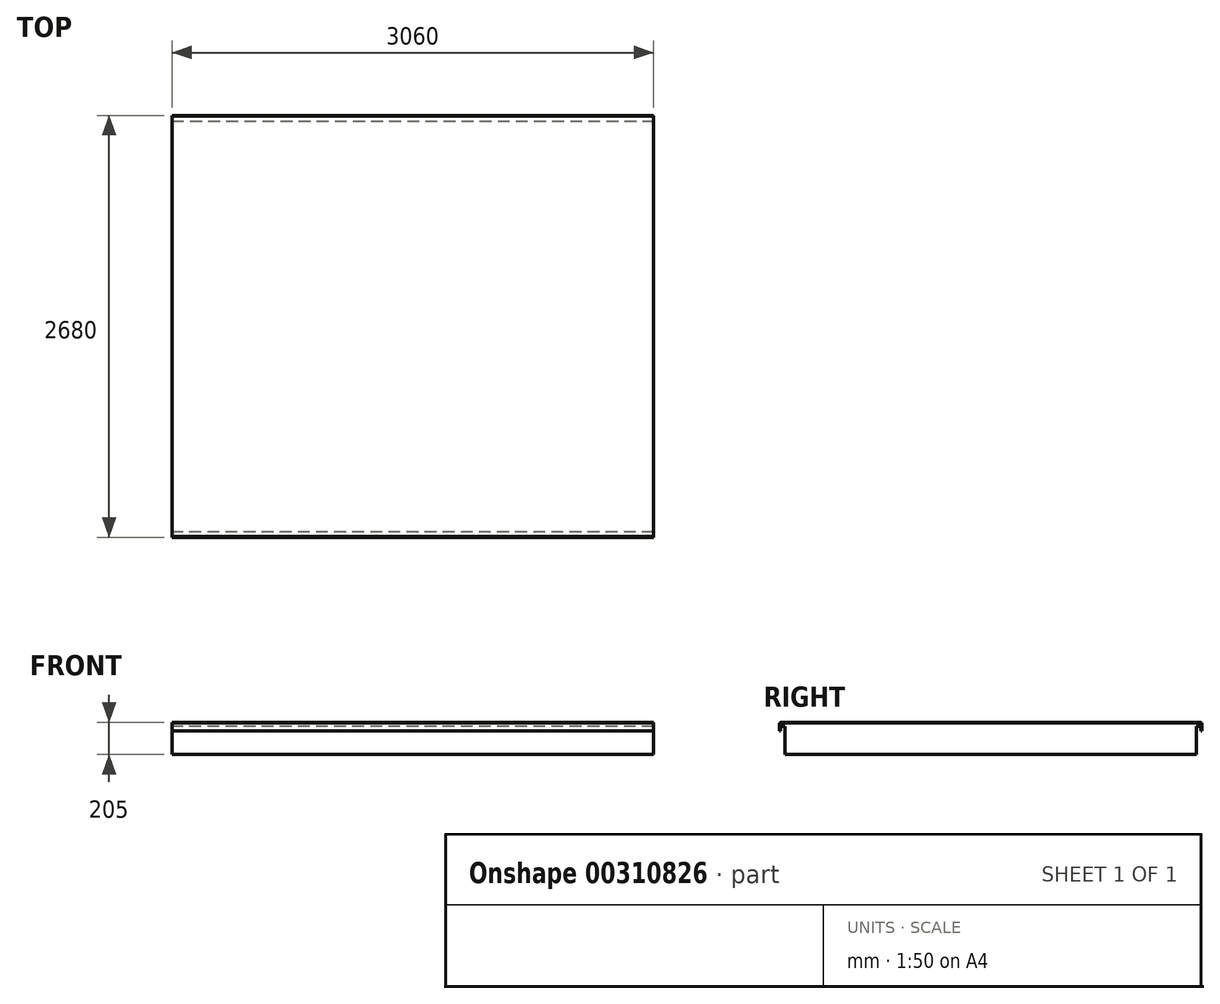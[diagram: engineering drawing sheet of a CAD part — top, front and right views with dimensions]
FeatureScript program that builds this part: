
annotation { "Feature Type Name" : "Feature", "Feature Type Description" : "" }
export const myFeature = defineFeature(function(context is Context, id is Id, definition is map)
    precondition{}
    {
        {
            var Q0;
            Q0=qCreatedBy(makeId("Top.planeOp"),FACE);
            var sketch = newSketch(context, id + "F0", { "sketchPlane" : qUnion([Q0])});
            skLineSegment(sketch, "E0.bottom", {"start": v(0, 0) * mm, "end": v(3060, 0) * mm});
            skLineSegment(sketch, "E0.top", {"start": v(0, 2670) * mm, "end": v(3060, 2670) * mm});
            skLineSegment(sketch, "E0.left", {"start": v(0, 0) * mm, "end": v(0, 2670) * mm});
            skLineSegment(sketch, "E0.right", {"start": v(3060, 0) * mm, "end": v(3060, 2670) * mm});
            skLineSegment(sketch, "E1", {"start": v(0, 2770) * mm, "end": v(3046.82, 2770) * mm, "construction": true});
            skSolve(sketch);
        }
        {
            var Q0;
            Q0=qSketchRegion(id+"F0",true);
            extrude(context, id + "F1", {"entities" : qUnion([Q0]), "depth" : 200 * mm});
        }
        {
            var Q0;
            Q0=qCreatedBy(makeId("Top.planeOp"),FACE);
            var sketch = newSketch(context, id + "F2", { "sketchPlane" : qUnion([Q0])});
            skSolve(sketch);
        }
        {
            var Q0;
            Q0=makeQuery(id+"F1.opExtrude","CAP_FACE",FACE,{"disambiguationData":[OSD([sQuery(id+"F0.wireOp",EDGE,"E0.bottom"),sQuery(id+"F0.wireOp",EDGE,"E0.top"),sQuery(id+"F0.wireOp",EDGE,"E0.left"),sQuery(id+"F0.wireOp",EDGE,"E0.right")])],"isStart":false});
            var sketch = newSketch(context, id + "F3", { "sketchPlane" : qUnion([Q0])});
            skLineSegment(sketch, "E2.bottom", {"start": v(0, 2670) * mm, "end": v(3060, 2670) * mm});
            skLineSegment(sketch, "E2.left", {"start": v(0, 2670) * mm, "end": v(0, 0) * mm});
            skLineSegment(sketch, "E2.right", {"start": v(3060, 2670) * mm, "end": v(3060, 0) * mm});
            skLineSegment(sketch, "E3", {"start": v(0, 0) * mm, "end": v(3060, 0) * mm});
            skSolve(sketch);
        }
        {
            var Q0;
            Q0=qSketchRegion(id+"F3",true);
            extrude(context, id + "F4", {"entities" : qUnion([Q0]), "depth" : 5 * mm});
        }
        {
            var Q0;
            Q0=makeQuery(id+"F3.imprint","IMPRINT",FACE,{"disambiguationData":[TD([[makeQuery(id+"F3.imprint","IMPRINT",EDGE,{"derivedFrom":sQuery(id+"F3.wireOp",EDGE,"E2.bottom")}),-1.0]])]});
            cPlane(context, id + "F5", {"entities" : qUnion([Q0]), "cplaneType" : CPlaneType.OFFSET, "offset" : 20 * mm, "oppositeDirection" : true, "width" : 150 * mm, "height" : 150 * mm});
        }
        {
            var Q0;
            Q0=qCreatedBy(makeId("Top.planeOp"),FACE);
            var sketch = newSketch(context, id + "F6", { "sketchPlane" : qUnion([Q0])});
            skLineSegment(sketch, "E4.bottom", {"start": v(0, 2670) * mm, "end": v(3060, 2670) * mm});
            skLineSegment(sketch, "E4.top", {"start": v(0, 2640) * mm, "end": v(3060, 2640) * mm});
            skLineSegment(sketch, "E4.left", {"start": v(0, 2670) * mm, "end": v(0, 2640) * mm});
            skLineSegment(sketch, "E4.right", {"start": v(3060, 2670) * mm, "end": v(3060, 2640) * mm});
            skLineSegment(sketch, "E5.bottom", {"start": v(3069.54, 0) * mm, "end": v(0, 0) * mm});
            skLineSegment(sketch, "E5.top", {"start": v(3069.54, 30) * mm, "end": v(0, 30) * mm});
            skLineSegment(sketch, "E5.left", {"start": v(3069.54, 0) * mm, "end": v(3069.54, 30) * mm});
            skLineSegment(sketch, "E5.right", {"start": v(0, 0) * mm, "end": v(0, 30) * mm});
            skSolve(sketch);
        }
        {
            var Q0;
            Q0=qSketchRegion(id+"F6",true);
            var Q1;
            Q1=qCreatedBy(id+"F5.planeOp",FACE);
            extrude(context, id + "F7", {"entities" : qUnion([Q0]), "operationType" : NewBodyOperationType.REMOVE, "endBound" : BoundingType.UP_TO_SURFACE, "endBoundEntityFace" : qUnion([Q1]), "depth" : 25 * mm});
        }
        {
            var Q0;
            Q0=makeQuery(id+"F1.opExtrude","SWEPT_FACE",FACE,{"disambiguationData":[OSD([sQuery(id+"F0.wireOp",EDGE,"E0.top")])]});
            var sketch = newSketch(context, id + "F8", { "sketchPlane" : qUnion([Q0])});
            skLineSegment(sketch, "E6.bottom", {"start": v(-3060, 200) * mm, "end": v(0, 200) * mm});
            skLineSegment(sketch, "E6.top", {"start": v(-3060, 150) * mm, "end": v(0, 150) * mm});
            skLineSegment(sketch, "E6.left", {"start": v(-3060, 200) * mm, "end": v(-3060, 150) * mm});
            skLineSegment(sketch, "E6.right", {"start": v(0, 200) * mm, "end": v(0, 150) * mm});
            skSolve(sketch);
        }
        {
            var Q0;
            Q0=qSketchRegion(id+"F8",true);
            extrude(context, id + "F9", {"entities" : qUnion([Q0]), "depth" : 5 * mm});
        }
        {
            var Q0;
            Q0=makeQuery(id+"F1.opExtrude","SWEPT_FACE",FACE,{"disambiguationData":[OSD([sQuery(id+"F0.wireOp",EDGE,"E0.bottom")])]});
            var sketch = newSketch(context, id + "F10", { "sketchPlane" : qUnion([Q0])});
            skLineSegment(sketch, "E7.bottom", {"start": v(0, 200) * mm, "end": v(3060, 200) * mm});
            skLineSegment(sketch, "E7.top", {"start": v(0, 150) * mm, "end": v(3060, 150) * mm});
            skLineSegment(sketch, "E7.left", {"start": v(0, 200) * mm, "end": v(0, 150) * mm});
            skLineSegment(sketch, "E7.right", {"start": v(3060, 200) * mm, "end": v(3060, 150) * mm});
            skSolve(sketch);
        }
        {
            var Q0;
            Q0 = qSketchRegion(id + "F10", true);
            extrude(context, id + "F11", {"entities" : qUnion([Q0]), "depth" : 5 * mm});
        }
    });
